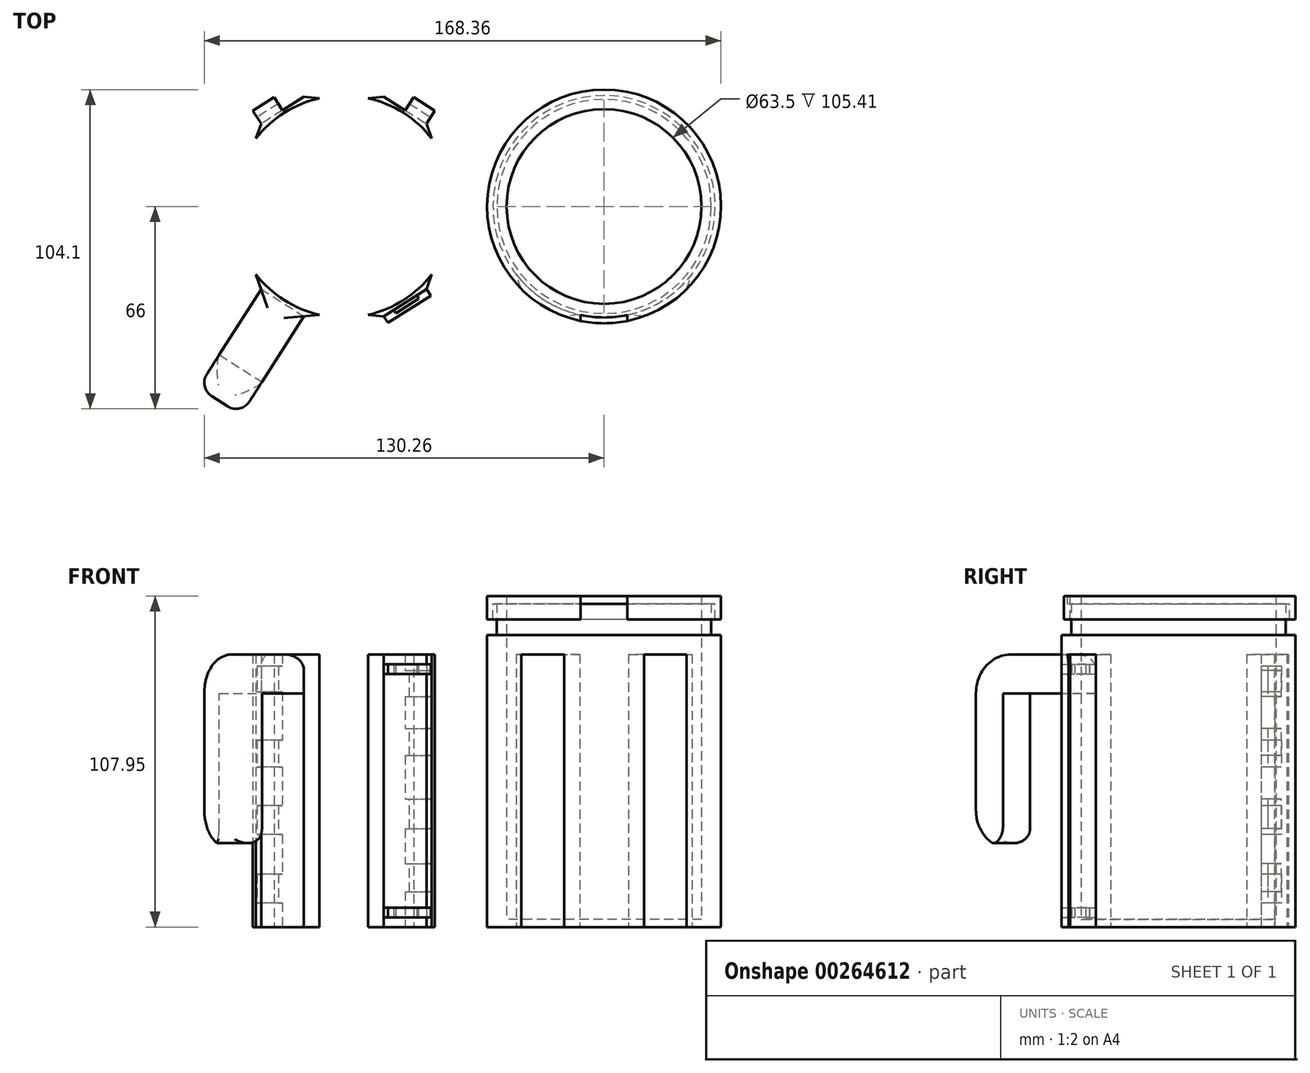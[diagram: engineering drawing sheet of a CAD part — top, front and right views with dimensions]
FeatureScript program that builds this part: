
annotation { "Feature Type Name" : "Feature", "Feature Type Description" : "" }
export const myFeature = defineFeature(function(context is Context, id is Id, definition is map)
    precondition{}
    {
        {
            var Q0;
            Q0=qCreatedBy(makeId("Top.planeOp"),FACE);
            var sketch = newSketch(context, id + "F0", { "sketchPlane" : qUnion([Q0])});
            skCircle(sketch, "E0", {"center": v(0, 0) * mm, "radius": 31.75 * mm});
            skCircle(sketch, "E1", {"center": v(0, 0) * mm, "radius": 38.1 * mm});
            skCircle(sketch, "E2", {"center": v(0, 0) * mm, "radius": 34.93 * mm});
            skCircle(sketch, "E3", {"center": v(0, 0) * mm, "radius": 36.2 * mm});
            skLineSegment(sketch, "E4", {"start": v(0, 0) * mm, "end": v(-26.94, -26.94) * mm});
            skLineSegment(sketch, "E5", {"start": v(0, 0) * mm, "end": v(26.94, -26.94) * mm});
            skLineSegment(sketch, "E6", {"start": v(0, 0) * mm, "end": v(-13.03, -35.8) * mm});
            skLineSegment(sketch, "E7", {"start": v(0, 0) * mm, "end": v(13.03, -35.8) * mm});
            skLineSegment(sketch, "E8", {"start": v(-26.94, -26.94) * mm, "end": v(-28.63, -22.15) * mm});
            skLineSegment(sketch, "E9", {"start": v(-7.98, -35.3) * mm, "end": v(-13.03, -35.8) * mm});
            skLineSegment(sketch, "E10", {"start": v(13.03, -35.8) * mm, "end": v(7.98, -35.3) * mm});
            skLineSegment(sketch, "E11", {"start": v(26.94, -26.94) * mm, "end": v(28.63, -22.15) * mm});
            skCircle(sketch, "E12", {"center": v(-84.78, 0) * mm, "radius": 38.1 * mm});
            skCircle(sketch, "E13", {"center": v(-84.78, 0) * mm, "radius": 36.2 * mm});
            skLineSegment(sketch, "E14", {"start": v(-84.78, 0) * mm, "end": v(-111.72, -26.94) * mm});
            skLineSegment(sketch, "E15", {"start": v(-84.78, 0) * mm, "end": v(-57.84, -26.94) * mm});
            skLineSegment(sketch, "E16", {"start": v(-84.78, 0) * mm, "end": v(-84.78, -38.1) * mm});
            skLineSegment(sketch, "E17", {"start": v(-84.78, 0) * mm, "end": v(-71.75, -35.8) * mm});
            skLineSegment(sketch, "E18", {"start": v(-84.78, 0) * mm, "end": v(-97.81, -35.8) * mm});
            skLineSegment(sketch, "E19", {"start": v(-111.72, -26.94) * mm, "end": v(-113.4, -22.15) * mm});
            skLineSegment(sketch, "E20", {"start": v(-97.81, -35.8) * mm, "end": v(-92.76, -35.3) * mm});
            skLineSegment(sketch, "E21", {"start": v(-71.75, -35.8) * mm, "end": v(-76.8, -35.3) * mm});
            skLineSegment(sketch, "E22", {"start": v(-57.84, -26.94) * mm, "end": v(-56.16, -22.15) * mm});
            skLineSegment(sketch, "E23", {"start": v(-111.72, -26.94) * mm, "end": v(-97.81, -35.8) * mm});
            skLineSegment(sketch, "E24", {"start": v(-71.75, -35.8) * mm, "end": v(-57.84, -26.94) * mm});
            skLineSegment(sketch, "E25", {"start": v(-84.78, 0) * mm, "end": v(-111.72, 26.94) * mm});
            skLineSegment(sketch, "E26", {"start": v(-84.78, 0) * mm, "end": v(-57.84, 26.94) * mm});
            skLineSegment(sketch, "E27", {"start": v(-84.78, 0) * mm, "end": v(-71.75, 35.8) * mm});
            skLineSegment(sketch, "E28", {"start": v(-84.78, 0) * mm, "end": v(-97.81, 35.8) * mm});
            skLineSegment(sketch, "E29", {"start": v(-84.78, 0) * mm, "end": v(-84.78, 38.1) * mm});
            skLineSegment(sketch, "E30", {"start": v(-111.72, 26.94) * mm, "end": v(-113.4, 22.15) * mm});
            skLineSegment(sketch, "E31", {"start": v(-97.81, 35.8) * mm, "end": v(-92.76, 35.3) * mm});
            skLineSegment(sketch, "E32", {"start": v(-71.75, 35.8) * mm, "end": v(-76.8, 35.3) * mm});
            skLineSegment(sketch, "E33", {"start": v(-57.84, 26.94) * mm, "end": v(-56.16, 22.15) * mm});
            skLineSegment(sketch, "E34", {"start": v(-57.84, 26.94) * mm, "end": v(-71.75, 35.8) * mm});
            skLineSegment(sketch, "E35", {"start": v(-97.81, 35.8) * mm, "end": v(-111.72, 26.94) * mm});
            skSolve(sketch);
        }
        {
            var Q0;
            Q0=makeQuery(id+"F0.imprint","IMPRINT",FACE,{"disambiguationData":[TD([[makeQuery(id+"F0.imprint","IMPRINT",EDGE,{"derivedFrom":sQuery(id+"F0.wireOp",EDGE,"E0")}),-1.0]])]});
            var Q1;
            {var subQ2=sQuery(id+"F0.wireOp",EDGE,"8zxYjvtb-MDoy-6YJJ-XKuE-w1UAtlA70Sip");Q1=makeQuery(id+"F0.imprint","IMPRINT",FACE,{"disambiguationData":[TD([[makeQuery(id+"F0.imprint","IMPRINT",EDGE,{"derivedFrom":subQ2}),1.0]])]});}
            var Q2;
            {var subQ0=sQuery(id+"F0.wireOp",EDGE,"h3sDWL1f-YZOR-unjp-TKPr-zdvw7zO6n5ZA");var subQ1=sQuery(id+"F0.wireOp",EDGE,"E1");var subQ2=makeQuery(id+"F0.imprint","INTERSECT",VERTEX,{"derivedFrom":[subQ1,subQ0]});Q2=makeQuery(id+"F0.imprint","IMPRINT",FACE,{"disambiguationData":[TD([[makeQuery(id+"F0.imprint","IMPRINT",EDGE,{"disambiguationData":[TD([[subQ2,1.0]])],"derivedFrom":subQ1}),1.0]])]});}
            var Q3;
            {var subQ0=sQuery(id+"F0.wireOp",EDGE,"h3sDWL1f-YZOR-unjp-TKPr-zdvw7zO6n5ZA");var subQ1=sQuery(id+"F0.wireOp",EDGE,"E1");var subQ2=makeQuery(id+"F0.imprint","INTERSECT",VERTEX,{"derivedFrom":[subQ1,subQ0]});Q3=makeQuery(id+"F0.imprint","IMPRINT",FACE,{"disambiguationData":[TD([[makeQuery(id+"F0.imprint","IMPRINT",EDGE,{"disambiguationData":[TD([[subQ2,-1.0]])],"derivedFrom":subQ1}),1.0]])]});}
            var Q4;
            {var subQ0=sQuery(id+"F0.wireOp",EDGE,"8zxYjvtb-MDoy-6YJJ-XKuE-w1UAtlA70Sip");Q4=makeQuery(id+"F0.imprint","IMPRINT",FACE,{"disambiguationData":[TD([[makeQuery(id+"F0.imprint","IMPRINT",EDGE,{"derivedFrom":subQ0}),-1.0]])]});}
            var Q5;
            {var subQ0=sQuery(id+"F0.wireOp",EDGE,"R7ShixpK-tb2N-bQR5-ACBT-eYuIy6adrrBf");var subQ1=sQuery(id+"F0.wireOp",EDGE,"E1");var subQ2=makeQuery(id+"F0.imprint","INTERSECT",VERTEX,{"derivedFrom":[subQ1,subQ0]});Q5=makeQuery(id+"F0.imprint","IMPRINT",FACE,{"disambiguationData":[TD([[makeQuery(id+"F0.imprint","IMPRINT",EDGE,{"disambiguationData":[TD([[subQ2,-1.0]])],"derivedFrom":subQ1}),1.0]])]});}
            var Q6;
            {var subQ0=sQuery(id+"F0.wireOp",EDGE,"C6yxxFIw-LrpI-xlVj-TdN5-gM4IXLVDDQ9a");Q6=makeQuery(id+"F0.imprint","IMPRINT",FACE,{"disambiguationData":[TD([[makeQuery(id+"F0.imprint","IMPRINT",EDGE,{"derivedFrom":subQ0}),-1.0]])]});}
            var Q7;
            {var subQ0=sQuery(id+"F0.wireOp",EDGE,"HXiYsXtY-R47m-jqzh-3tiA-JMCs7zAql3W5");var subQ1=sQuery(id+"F0.wireOp",EDGE,"E1");var subQ2=makeQuery(id+"F0.imprint","INTERSECT",VERTEX,{"derivedFrom":[subQ1,subQ0]});Q7=makeQuery(id+"F0.imprint","IMPRINT",FACE,{"disambiguationData":[TD([[makeQuery(id+"F0.imprint","IMPRINT",EDGE,{"disambiguationData":[TD([[subQ2,-1.0]])],"derivedFrom":subQ1}),1.0]])]});}
            var Q8;
            {var subQ0=sQuery(id+"F0.wireOp",EDGE,"HJ59A699-sTLV-QdIX-rFf9-DagDQaaTut5k");Q8=makeQuery(id+"F0.imprint","IMPRINT",FACE,{"disambiguationData":[TD([[makeQuery(id+"F0.imprint","IMPRINT",EDGE,{"derivedFrom":subQ0}),1.0]])]});}
            var Q9;
            Q9=makeQuery(id+"F0.imprint","IMPRINT",FACE,{"disambiguationData":[TD([[makeQuery(id+"F0.imprint","IMPRINT",EDGE,{"derivedFrom":sQuery(id+"F0.wireOp",EDGE,"E2")}),-1.0]])]});
            var Q10;
            {var subQ0=sQuery(id+"F0.wireOp",EDGE,"E8");Q10=makeQuery(id+"F0.imprint","IMPRINT",FACE,{"disambiguationData":[TD([[makeQuery(id+"F0.imprint","IMPRINT",EDGE,{"derivedFrom":subQ0}),-1.0]])]});}
            var Q11;
            {var subQ0=sQuery(id+"F0.wireOp",EDGE,"E9");Q11=makeQuery(id+"F0.imprint","IMPRINT",FACE,{"disambiguationData":[TD([[makeQuery(id+"F0.imprint","IMPRINT",EDGE,{"derivedFrom":subQ0}),-1.0]])]});}
            var Q12;
            {var subQ0=sQuery(id+"F0.wireOp",EDGE,"E10");Q12=makeQuery(id+"F0.imprint","IMPRINT",FACE,{"disambiguationData":[TD([[makeQuery(id+"F0.imprint","IMPRINT",EDGE,{"derivedFrom":subQ0}),-1.0]])]});}
            var Q13;
            {var subQ0=sQuery(id+"F0.wireOp",EDGE,"E11");Q13=makeQuery(id+"F0.imprint","IMPRINT",FACE,{"disambiguationData":[TD([[makeQuery(id+"F0.imprint","IMPRINT",EDGE,{"derivedFrom":subQ0}),1.0]])]});}
            var Q14;
            {var subQ5=sQuery(id+"F0.wireOp",EDGE,"E6");var subQ7=sQuery(id+"F0.wireOp",EDGE,"E2");var subQ8=makeQuery(id+"F0.imprint","INTERSECT",VERTEX,{"derivedFrom":[subQ7,subQ5]});Q14=makeQuery(id+"F0.imprint","IMPRINT",FACE,{"disambiguationData":[TD([[makeQuery(id+"F0.imprint","IMPRINT",EDGE,{"disambiguationData":[TD([[subQ8,-1.0]])],"derivedFrom":subQ7}),-1.0]])]});}
            var Q15;
            {var subQ5=sQuery(id+"F0.wireOp",EDGE,"E4");var subQ7=sQuery(id+"F0.wireOp",EDGE,"E2");var subQ8=makeQuery(id+"F0.imprint","INTERSECT",VERTEX,{"derivedFrom":[subQ7,subQ5]});Q15=makeQuery(id+"F0.imprint","IMPRINT",FACE,{"disambiguationData":[TD([[makeQuery(id+"F0.imprint","IMPRINT",EDGE,{"disambiguationData":[TD([[subQ8,1.0]])],"derivedFrom":subQ7}),-1.0]])]});}
            extrude(context, id + "F1", {"entities" : qUnion([Q0, Q1, Q2, Q3, Q4, Q5, Q6, Q7, Q8, Q9, Q10, Q11, Q12, Q13, Q14, Q15]), "depth" : 95.25 * mm});
        }
        {
            var Q0;
            Q0=makeQuery(id+"F0.imprint","IMPRINT",FACE,{"disambiguationData":[TD([[makeQuery(id+"F0.imprint","IMPRINT",EDGE,{"derivedFrom":sQuery(id+"F0.wireOp",EDGE,"E0")}),-1.0]])]});
            extrude(context, id + "F2", {"entities" : qUnion([Q0]), "operationType" : NewBodyOperationType.ADD, "depth" : 107.95 * mm});
        }
        {
            var Q0;
            Q0=makeQuery(id+"F2.opExtrude","CAP_FACE",FACE,{"disambiguationData":[OSD([sQuery(id+"F0.wireOp",EDGE,"E0"),sQuery(id+"F0.wireOp",EDGE,"E2")])],"isStart":false});
            var sketch = newSketch(context, id + "F3", { "sketchPlane" : qUnion([Q0])});
            skCircle(sketch, "E36", {"center": v(0, 0) * mm, "radius": 36.2 * mm});
            skCircle(sketch, "E37", {"center": v(0, 0) * mm, "radius": 38.1 * mm});
            skLineSegment(sketch, "E38.left", {"start": v(-7.62, -35.38) * mm, "end": v(-7.62, -37.33) * mm});
            skLineSegment(sketch, "E38.right", {"start": v(7.62, -35.38) * mm, "end": v(7.62, -37.33) * mm});
            skPoint(sketch, "E39.orphan", {"position": v(7.62, 0) * mm});
            skPoint(sketch, "E40.orphan", {"position": v(-7.62, 0) * mm});
            skSolve(sketch);
        }
        {
            var Q0;
            Q0=makeQuery(id+"F3.imprint","IMPRINT",FACE,{"disambiguationData":[TD([[makeQuery(id+"F3.imprint","IMPRINT",EDGE,{"derivedFrom":sQuery(id+"F3.wireOp",EDGE,"E36")}),1.0]])]});
            extrude(context, id + "F4", {"entities" : qUnion([Q0]), "operationType" : NewBodyOperationType.ADD, "oppositeDirection" : true, "depth" : 2.54 * mm});
        }
        {
            var Q0;
            Q0=makeQuery(id+"F3.imprint","IMPRINT",FACE,{"disambiguationData":[TD([[makeQuery(id+"F3.imprint","IMPRINT",EDGE,{"derivedFrom":sQuery(id+"F3.wireOp",EDGE,"E36")}),-1.0]])]});
            extrude(context, id + "F5", {"entities" : qUnion([Q0]), "operationType" : NewBodyOperationType.ADD, "oppositeDirection" : true, "depth" : 7.62 * mm});
        }
        {
            var Q0;
            {var subQ0=sQuery(id+"F3.wireOp",EDGE,"E38.left");Q0=makeQuery(id+"F3.imprint","IMPRINT",FACE,{"disambiguationData":[TD([[makeQuery(id+"F3.imprint","IMPRINT",EDGE,{"derivedFrom":subQ0}),1.0]])]});}
            extrude(context, id + "F6", {"entities" : qUnion([Q0]), "operationType" : NewBodyOperationType.REMOVE, "oppositeDirection" : true, "depth" : 7.62 * mm});
        }
        {
            var Q0;
            {var subQ0=sQuery(id+"F0.wireOp",EDGE,"E8");Q0=makeQuery(id+"F0.imprint","IMPRINT",FACE,{"disambiguationData":[TD([[makeQuery(id+"F0.imprint","IMPRINT",EDGE,{"derivedFrom":subQ0}),-1.0]])]});}
            var Q1;
            {var subQ0=sQuery(id+"F0.wireOp",EDGE,"E4");var subQ5=sQuery(id+"F0.wireOp",EDGE,"E3");var subQ6=makeQuery(id+"F0.imprint","INTERSECT",VERTEX,{"derivedFrom":[subQ5,subQ0]});Q1=makeQuery(id+"F0.imprint","IMPRINT",FACE,{"disambiguationData":[TD([[makeQuery(id+"F0.imprint","IMPRINT",EDGE,{"disambiguationData":[TD([[subQ6,-1.0]])],"derivedFrom":subQ5}),-1.0]])]});}
            var Q2;
            {var subQ0=sQuery(id+"F0.wireOp",EDGE,"E9");Q2=makeQuery(id+"F0.imprint","IMPRINT",FACE,{"disambiguationData":[TD([[makeQuery(id+"F0.imprint","IMPRINT",EDGE,{"derivedFrom":subQ0}),-1.0]])]});}
            var Q3;
            {var subQ0=sQuery(id+"F0.wireOp",EDGE,"E10");Q3=makeQuery(id+"F0.imprint","IMPRINT",FACE,{"disambiguationData":[TD([[makeQuery(id+"F0.imprint","IMPRINT",EDGE,{"derivedFrom":subQ0}),-1.0]])]});}
            var Q4;
            {var subQ3=sQuery(id+"F0.wireOp",EDGE,"E7");var subQ5=sQuery(id+"F0.wireOp",EDGE,"E3");var subQ6=makeQuery(id+"F0.imprint","INTERSECT",VERTEX,{"derivedFrom":[subQ5,subQ3]});Q4=makeQuery(id+"F0.imprint","IMPRINT",FACE,{"disambiguationData":[TD([[makeQuery(id+"F0.imprint","IMPRINT",EDGE,{"disambiguationData":[TD([[subQ6,-1.0]])],"derivedFrom":subQ5}),-1.0]])]});}
            var Q5;
            {var subQ0=sQuery(id+"F0.wireOp",EDGE,"E11");Q5=makeQuery(id+"F0.imprint","IMPRINT",FACE,{"disambiguationData":[TD([[makeQuery(id+"F0.imprint","IMPRINT",EDGE,{"derivedFrom":subQ0}),1.0]])]});}
            extrude(context, id + "F7", {"entities" : qUnion([Q0, Q1, Q2, Q3, Q4, Q5]), "operationType" : NewBodyOperationType.REMOVE, "depth" : 88.9 * mm});
        }
        {
            var Q0;
            {var subQ0=sQuery(id+"F0.wireOp",EDGE,"E14");var subQ5=sQuery(id+"F0.wireOp",EDGE,"E13");var subQ6=makeQuery(id+"F0.imprint","INTERSECT",VERTEX,{"derivedFrom":[subQ5,subQ0]});Q0=makeQuery(id+"F0.imprint","IMPRINT",FACE,{"disambiguationData":[TD([[makeQuery(id+"F0.imprint","IMPRINT",EDGE,{"disambiguationData":[TD([[subQ6,-1.0]])],"derivedFrom":subQ5}),-1.0]])]});}
            var Q1;
            {var subQ0=sQuery(id+"F0.wireOp",EDGE,"E19");Q1=makeQuery(id+"F0.imprint","IMPRINT",FACE,{"disambiguationData":[TD([[makeQuery(id+"F0.imprint","IMPRINT",EDGE,{"derivedFrom":subQ0}),-1.0]])]});}
            var Q2;
            {var subQ0=sQuery(id+"F0.wireOp",EDGE,"E20");Q2=makeQuery(id+"F0.imprint","IMPRINT",FACE,{"disambiguationData":[TD([[makeQuery(id+"F0.imprint","IMPRINT",EDGE,{"derivedFrom":subQ0}),1.0]])]});}
            var Q3;
            {var subQ0=sQuery(id+"F0.wireOp",EDGE,"E21");Q3=makeQuery(id+"F0.imprint","IMPRINT",FACE,{"disambiguationData":[TD([[makeQuery(id+"F0.imprint","IMPRINT",EDGE,{"derivedFrom":subQ0}),-1.0]])]});}
            var Q4;
            {var subQ3=sQuery(id+"F0.wireOp",EDGE,"E17");var subQ5=sQuery(id+"F0.wireOp",EDGE,"E13");var subQ7=makeQuery(id+"F0.imprint","INTERSECT",VERTEX,{"derivedFrom":[subQ5,subQ3]});Q4=makeQuery(id+"F0.imprint","IMPRINT",FACE,{"disambiguationData":[TD([[makeQuery(id+"F0.imprint","IMPRINT",EDGE,{"disambiguationData":[TD([[subQ7,-1.0]])],"derivedFrom":subQ5}),-1.0]])]});}
            var Q5;
            {var subQ0=sQuery(id+"F0.wireOp",EDGE,"E22");Q5=makeQuery(id+"F0.imprint","IMPRINT",FACE,{"disambiguationData":[TD([[makeQuery(id+"F0.imprint","IMPRINT",EDGE,{"derivedFrom":subQ0}),1.0]])]});}
            extrude(context, id + "F8", {"entities" : qUnion([Q0, Q1, Q2, Q3, Q4, Q5]), "operationType" : NewBodyOperationType.ADD, "depth" : 88.9 * mm});
        }
        {
            var Q0;
            Q0=makeQuery(id+"F8.opExtrude","SWEPT_FACE",FACE,{"disambiguationData":[OSD([sQuery(id+"F0.wireOp",EDGE,"E23")])]});
            var sketch = newSketch(context, id + "F9", { "sketchPlane" : qUnion([Q0])});
            skLineSegment(sketch, "E41", {"start": v(-79.75, 76.2) * mm, "end": v(-63.26, 76.2) * mm});
            skSolve(sketch);
        }
        {
            var Q0;
            {var subQ0=sQuery(id+"F9.wireOp",EDGE,"E41");Q0=makeQuery(id+"F9.imprint","IMPRINT",FACE,{"disambiguationData":[TD([[makeQuery(id+"F9.imprint","IMPRINT",EDGE,{"derivedFrom":subQ0}),1.0]])]});}
            extrude(context, id + "F10", {"entities" : qUnion([Q0]), "operationType" : NewBodyOperationType.ADD, "depth" : 38.1 * mm});
        }
        {
            var Q0;
            Q0=makeQuery(id+"F10.opExtrude","SWEPT_FACE",FACE,{"disambiguationData":[OSD([sQuery(id+"F9.wireOp",EDGE,"E41")])]});
            var sketch = newSketch(context, id + "F11", { "sketchPlane" : qUnion([Q0])});
            skLineSegment(sketch, "E42", {"start": v(-125.37, 48.36) * mm, "end": v(-111.46, 57.22) * mm});
            skSolve(sketch);
        }
        {
            var Q0;
            {var subQ0=sQuery(id+"F11.wireOp",EDGE,"E42");Q0=makeQuery(id+"F11.imprint","IMPRINT",FACE,{"disambiguationData":[TD([[makeQuery(id+"F11.imprint","IMPRINT",EDGE,{"derivedFrom":subQ0}),1.0]])]});}
            extrude(context, id + "F12", {"entities" : qUnion([Q0]), "operationType" : NewBodyOperationType.ADD, "depth" : 50.8 * mm});
        }
        {
            var Q0;
            Q0=makeQuery(id+"F10.opExtrude","CAP_EDGE",EDGE,{"disambiguationData":[OSD([sQuery(id+"F9.wireOp",EDGE,"E41")])],"isStart":true});
            var Q1;
            Q1=makeQuery(id+"F12.opExtrude","CAP_EDGE",EDGE,{"disambiguationData":[OSD([sQuery(id+"F11.wireOp",EDGE,"E42")])],"isStart":true});
            var Q2;
            Q2=makeQuery(id+"F10.opExtrude","CAP_EDGE",EDGE,{"disambiguationData":[OSD([sQuery(id+"F0.wireOp",EDGE,"E23")])],"isStart":false});
            var Q3;
            Q3=makeQuery(id+"F12.opExtrude","CAP_EDGE",EDGE,{"disambiguationData":[OSD([sQuery(id+"F9.wireOp",EDGE,"E41")])],"isStart":false});
            fillet(context, id + "F13", {"entities" : qUnion([Q0, Q1, Q2, Q3]), "radius" : 12.7 * mm, "tangentPropagation" : true, "allowEdgeOverflow" : false});
        }
        {
            var Q0;
            {var subQ0=sQuery(id+"F0.wireOp",EDGE,"E23");var subQ1=sQuery(id+"F0.wireOp",EDGE,"E19");var subQ2=sQuery(id+"F0.wireOp",EDGE,"E14");var subQ3=sQuery(id+"F0.wireOp",EDGE,"E12");Q0=makeQuery(id+"F12.boolean.opBoolean","MERGE",EDGE,{"derivedFrom":[makeQuery(id+"F10.opExtrude","CAP_EDGE",EDGE,{"disambiguationData":[OSD([subQ3,subQ2,subQ1,subQ0])],"isStart":false}),makeQuery(id+"F12.opExtrude","SWEPT_EDGE",EDGE,{"disambiguationData":[OSD([subQ3,subQ2,subQ1,subQ0,sQuery(id+"F9.wireOp",EDGE,"E41")])]})]});}
            var Q1;
            {var subQ0=sQuery(id+"F0.wireOp",EDGE,"E23");var subQ1=sQuery(id+"F0.wireOp",EDGE,"E20");var subQ2=sQuery(id+"F0.wireOp",EDGE,"E18");var subQ3=sQuery(id+"F0.wireOp",EDGE,"E12");Q1=makeQuery(id+"F12.boolean.opBoolean","MERGE",EDGE,{"derivedFrom":[makeQuery(id+"F10.opExtrude","CAP_EDGE",EDGE,{"disambiguationData":[OSD([subQ3,subQ2,subQ1,subQ0])],"isStart":false}),makeQuery(id+"F12.opExtrude","SWEPT_EDGE",EDGE,{"disambiguationData":[OSD([subQ3,subQ2,subQ1,subQ0,sQuery(id+"F9.wireOp",EDGE,"E41")])]})]});}
            var Q2;
            {var subQ0=sQuery(id+"F9.wireOp",EDGE,"E41");var subQ1=sQuery(id+"F0.wireOp",EDGE,"E23");var subQ2=sQuery(id+"F0.wireOp",EDGE,"E19");var subQ3=sQuery(id+"F0.wireOp",EDGE,"E14");var subQ4=sQuery(id+"F0.wireOp",EDGE,"E12");Q2=makeQuery(id+"F13.opFillet","BLEND_EDGE",EDGE,{"blendedFrom":[makeQuery(id+"F10.opExtrude","CAP_EDGE",EDGE,{"disambiguationData":[OSD([subQ0])],"isStart":true}),makeQuery(id+"F12.boolean.opBoolean","MERGE",FACE,{"derivedFrom":[makeQuery(id+"F10.opExtrude","SWEPT_FACE",FACE,{"disambiguationData":[OSD([subQ4,subQ3,subQ2,subQ1])]}),makeQuery(id+"F12.opExtrude","SWEPT_FACE",FACE,{"disambiguationData":[OSD([subQ4,subQ3,subQ2,subQ1,subQ0])]})]})],"blendedInto":[makeQuery(id+"F12.boolean.opBoolean","MERGE",FACE,{"derivedFrom":[makeQuery(id+"F10.opExtrude","SWEPT_FACE",FACE,{"disambiguationData":[OSD([subQ4,subQ3,subQ2,subQ1])]}),makeQuery(id+"F12.opExtrude","SWEPT_FACE",FACE,{"disambiguationData":[OSD([subQ4,subQ3,subQ2,subQ1,subQ0])]})]})]});}
            var Q3;
            Q3=makeQuery(id+"F13.opFillet","BLEND_EDGE",EDGE,{"blendedFrom":[makeQuery(id+"F12.opExtrude","CAP_EDGE",EDGE,{"disambiguationData":[OSD([sQuery(id+"F9.wireOp",EDGE,"E41")])],"isStart":false}),makeQuery(id+"F12.opExtrude","SWEPT_FACE",FACE,{"disambiguationData":[OSD([sQuery(id+"F11.wireOp",EDGE,"E42")])]})],"blendedInto":[makeQuery(id+"F12.opExtrude","SWEPT_FACE",FACE,{"disambiguationData":[OSD([sQuery(id+"F11.wireOp",EDGE,"E42")])]})]});
            fillet(context, id + "F14", {"entities" : qUnion([Q0, Q1, Q2, Q3]), "radius" : 5.08 * mm, "tangentPropagation" : true, "allowEdgeOverflow" : false});
        }
        {
            var Q0;
            Q0=makeQuery(id+"F8.opExtrude","SWEPT_FACE",FACE,{"disambiguationData":[OSD([sQuery(id+"F0.wireOp",EDGE,"E24")])]});
            var sketch = newSketch(context, id + "F15", { "sketchPlane" : qUnion([Q0])});
            skLineSegment(sketch, "E43", {"start": v(-75.94, 88.9) * mm, "end": v(-75.94, 82.55) * mm});
            skLineSegment(sketch, "E44", {"start": v(-67.07, 88.9) * mm, "end": v(-67.07, 82.55) * mm});
            skLineSegment(sketch, "E45", {"start": v(-79.75, 82.55) * mm, "end": v(-63.26, 82.55) * mm});
            skLineSegment(sketch, "E46", {"start": v(-79.75, 85.73) * mm, "end": v(-63.26, 85.73) * mm});
            skPoint(sketch, "E46.startSnap0", {"position": v(-75.94, 85.73) * mm});
            skLineSegment(sketch, "E47", {"start": v(-79.75, 6.35) * mm, "end": v(-63.26, 6.35) * mm});
            skLineSegment(sketch, "E48", {"start": v(-75.94, 6.35) * mm, "end": v(-75.94, 0) * mm});
            skLineSegment(sketch, "E49", {"start": v(-67.07, 6.35) * mm, "end": v(-67.07, 0) * mm});
            skLineSegment(sketch, "E50", {"start": v(-67.07, 3.18) * mm, "end": v(-63.26, 3.17) * mm});
            skLineSegment(sketch, "E51", {"start": v(-67.07, 3.18) * mm, "end": v(-79.75, 3.17) * mm});
            skSolve(sketch);
        }
        {
            var Q0;
            {var subQ0=sQuery(id+"F15.wireOp",EDGE,"E45");var subQ1=sQuery(id+"F15.wireOp",EDGE,"E43");var subQ2=makeQuery(id+"F15.imprint","INTERSECT",VERTEX,{"derivedFrom":[subQ1,subQ0]});Q0=makeQuery(id+"F15.imprint","IMPRINT",FACE,{"disambiguationData":[TD([[makeQuery(id+"F15.imprint","IMPRINT",EDGE,{"disambiguationData":[TD([[subQ2,1.0]])],"derivedFrom":subQ1}),-1.0]])]});}
            var Q1;
            {var subQ0=sQuery(id+"F15.wireOp",EDGE,"E45");var subQ1=sQuery(id+"F15.wireOp",EDGE,"E44");var subQ2=makeQuery(id+"F15.imprint","INTERSECT",VERTEX,{"derivedFrom":[subQ1,subQ0]});Q1=makeQuery(id+"F15.imprint","IMPRINT",FACE,{"disambiguationData":[TD([[makeQuery(id+"F15.imprint","IMPRINT",EDGE,{"disambiguationData":[TD([[subQ2,1.0]])],"derivedFrom":subQ1}),1.0]])]});}
            extrude(context, id + "F16", {"entities" : qUnion([Q0, Q1]), "operationType" : NewBodyOperationType.ADD, "depth" : 2.54 * mm});
        }
        {
            var Q0;
            Q0=makeQuery(id+"F16.opExtrude","SWEPT_FACE",FACE,{"disambiguationData":[OSD([sQuery(id+"F15.wireOp",EDGE,"E43")])]});
            var sketch = newSketch(context, id + "F17", { "sketchPlane" : qUnion([Q0])});
            skLineSegment(sketch, "E52", {"start": v(7.09, 85.73) * mm, "end": v(7.09, 82.55) * mm});
            skSolve(sketch);
        }
        {
            var Q0;
            {var subQ0=sQuery(id+"F17.wireOp",EDGE,"E52");Q0=makeQuery(id+"F17.imprint","IMPRINT",FACE,{"disambiguationData":[TD([[makeQuery(id+"F17.imprint","IMPRINT",EDGE,{"derivedFrom":subQ0}),-1.0]])]});}
            extrude(context, id + "F18", {"entities" : qUnion([Q0]), "operationType" : NewBodyOperationType.ADD, "depth" : 10.16 * mm});
        }
        {
            var Q0;
            {var subQ0=sQuery(id+"F15.wireOp",EDGE,"E47");var subQ3=sQuery(id+"F15.wireOp",EDGE,"E48");var subQ4=makeQuery(id+"F15.imprint","INTERSECT",VERTEX,{"derivedFrom":[subQ0,subQ3]});Q0=makeQuery(id+"F15.imprint","IMPRINT",FACE,{"disambiguationData":[TD([[makeQuery(id+"F15.imprint","IMPRINT",EDGE,{"disambiguationData":[TD([[subQ4,-1.0]])],"derivedFrom":subQ3}),-1.0]])]});}
            var Q1;
            {var subQ5=sQuery(id+"F15.wireOp",EDGE,"E50");Q1=makeQuery(id+"F15.imprint","IMPRINT",FACE,{"disambiguationData":[TD([[makeQuery(id+"F15.imprint","IMPRINT",EDGE,{"derivedFrom":subQ5}),1.0]])]});}
            extrude(context, id + "F19", {"entities" : qUnion([Q0, Q1]), "operationType" : NewBodyOperationType.ADD, "depth" : 2.54 * mm});
        }
        {
            var Q0;
            Q0=makeQuery(id+"F19.opExtrude","SWEPT_FACE",FACE,{"disambiguationData":[OSD([sQuery(id+"F15.wireOp",EDGE,"E48")])]});
            var sketch = newSketch(context, id + "F20", { "sketchPlane" : qUnion([Q0])});
            skLineSegment(sketch, "E53", {"start": v(7.09, 6.35) * mm, "end": v(7.09, 3.17) * mm});
            skSolve(sketch);
        }
        {
            var Q0;
            {var subQ0=sQuery(id+"F20.wireOp",EDGE,"E53");Q0=makeQuery(id+"F20.imprint","IMPRINT",FACE,{"disambiguationData":[TD([[makeQuery(id+"F20.imprint","IMPRINT",EDGE,{"derivedFrom":subQ0}),-1.0]])]});}
            extrude(context, id + "F21", {"entities" : qUnion([Q0]), "operationType" : NewBodyOperationType.ADD, "depth" : 10.16 * mm});
        }
        {
            var Q0;
            {var subQ3=sQuery(id+"F0.wireOp",EDGE,"E28");var subQ5=sQuery(id+"F0.wireOp",EDGE,"E13");var subQ6=makeQuery(id+"F0.imprint","INTERSECT",VERTEX,{"derivedFrom":[subQ5,subQ3]});Q0=makeQuery(id+"F0.imprint","IMPRINT",FACE,{"disambiguationData":[TD([[makeQuery(id+"F0.imprint","IMPRINT",EDGE,{"disambiguationData":[TD([[subQ6,-1.0]])],"derivedFrom":subQ5}),-1.0]])]});}
            var Q1;
            {var subQ0=sQuery(id+"F0.wireOp",EDGE,"E30");Q1=makeQuery(id+"F0.imprint","IMPRINT",FACE,{"disambiguationData":[TD([[makeQuery(id+"F0.imprint","IMPRINT",EDGE,{"derivedFrom":subQ0}),1.0]])]});}
            var Q2;
            {var subQ0=sQuery(id+"F0.wireOp",EDGE,"E31");Q2=makeQuery(id+"F0.imprint","IMPRINT",FACE,{"disambiguationData":[TD([[makeQuery(id+"F0.imprint","IMPRINT",EDGE,{"derivedFrom":subQ0}),-1.0]])]});}
            var Q3;
            {var subQ0=sQuery(id+"F0.wireOp",EDGE,"E32");Q3=makeQuery(id+"F0.imprint","IMPRINT",FACE,{"disambiguationData":[TD([[makeQuery(id+"F0.imprint","IMPRINT",EDGE,{"derivedFrom":subQ0}),1.0]])]});}
            var Q4;
            {var subQ0=sQuery(id+"F0.wireOp",EDGE,"E26");var subQ5=sQuery(id+"F0.wireOp",EDGE,"E13");var subQ6=makeQuery(id+"F0.imprint","INTERSECT",VERTEX,{"derivedFrom":[subQ5,subQ0]});Q4=makeQuery(id+"F0.imprint","IMPRINT",FACE,{"disambiguationData":[TD([[makeQuery(id+"F0.imprint","IMPRINT",EDGE,{"disambiguationData":[TD([[subQ6,-1.0]])],"derivedFrom":subQ5}),-1.0]])]});}
            var Q5;
            {var subQ0=sQuery(id+"F0.wireOp",EDGE,"E33");Q5=makeQuery(id+"F0.imprint","IMPRINT",FACE,{"disambiguationData":[TD([[makeQuery(id+"F0.imprint","IMPRINT",EDGE,{"derivedFrom":subQ0}),-1.0]])]});}
            extrude(context, id + "F22", {"entities" : qUnion([Q0, Q1, Q2, Q3, Q4, Q5]), "depth" : 88.9 * mm});
        }
        {
            var Q0;
            Q0=makeQuery(id+"F22.opExtrude","SWEPT_FACE",FACE,{"disambiguationData":[OSD([sQuery(id+"F0.wireOp",EDGE,"E35")])]});
            var sketch = newSketch(context, id + "F23", { "sketchPlane" : qUnion([Q0])});
            skLineSegment(sketch, "E54", {"start": v(71.5, 88.9) * mm, "end": v(71.5, 0) * mm});
            skSolve(sketch);
        }
        {
            var Q0;
            {var subQ0=sQuery(id+"F23.wireOp",EDGE,"E54");Q0=makeQuery(id+"F23.imprint","IMPRINT",FACE,{"disambiguationData":[TD([[makeQuery(id+"F23.imprint","IMPRINT",EDGE,{"derivedFrom":subQ0}),1.0]])]});}
            extrude(context, id + "F24", {"entities" : qUnion([Q0]), "operationType" : NewBodyOperationType.ADD, "depth" : 5.08 * mm});
        }
        {
            var Q0;
            Q0=makeQuery(id+"F24.opExtrude","SWEPT_FACE",FACE,{"disambiguationData":[OSD([sQuery(id+"F0.wireOp",EDGE,"E12"),sQuery(id+"F0.wireOp",EDGE,"E25"),sQuery(id+"F0.wireOp",EDGE,"E30"),sQuery(id+"F0.wireOp",EDGE,"E35")])]});
            var sketch = newSketch(context, id + "F25", { "sketchPlane" : qUnion([Q0])});
            skLineSegment(sketch, "E55", {"start": v(-85.3, 88.9) * mm, "end": v(-85.3, 0) * mm});
            skLineSegment(sketch, "E56", {"start": v(-85.3, 85.05) * mm, "end": v(-82.75, 85.05) * mm});
            skLineSegment(sketch, "E57", {"start": v(-85.3, 76.63) * mm, "end": v(-82.75, 76.63) * mm});
            skLineSegment(sketch, "E58", {"start": v(-85.3, 60.95) * mm, "end": v(-82.75, 60.95) * mm});
            skLineSegment(sketch, "E59", {"start": v(-85.3, 52.14) * mm, "end": v(-82.75, 52.14) * mm});
            skLineSegment(sketch, "E60", {"start": v(-85.3, 39.6) * mm, "end": v(-82.75, 39.6) * mm});
            skLineSegment(sketch, "E61", {"start": v(-85.3, 30.19) * mm, "end": v(-82.75, 30.19) * mm});
            skLineSegment(sketch, "E62", {"start": v(-85.3, 17.26) * mm, "end": v(-82.75, 17.26) * mm});
            skLineSegment(sketch, "E63", {"start": v(-85.3, 7.86) * mm, "end": v(-82.75, 7.86) * mm});
            skSolve(sketch);
        }
        {
            var Q0;
            {var subQ0=sQuery(id+"F25.wireOp",EDGE,"E58");Q0=makeQuery(id+"F25.imprint","IMPRINT",FACE,{"disambiguationData":[TD([[makeQuery(id+"F25.imprint","IMPRINT",EDGE,{"derivedFrom":subQ0}),-1.0]])]});}
            var Q1;
            {var subQ0=sQuery(id+"F25.wireOp",EDGE,"E56");Q1=makeQuery(id+"F25.imprint","IMPRINT",FACE,{"disambiguationData":[TD([[makeQuery(id+"F25.imprint","IMPRINT",EDGE,{"derivedFrom":subQ0}),-1.0]])]});}
            var Q2;
            {var subQ0=sQuery(id+"F25.wireOp",EDGE,"E60");Q2=makeQuery(id+"F25.imprint","IMPRINT",FACE,{"disambiguationData":[TD([[makeQuery(id+"F25.imprint","IMPRINT",EDGE,{"derivedFrom":subQ0}),-1.0]])]});}
            var Q3;
            {var subQ0=sQuery(id+"F25.wireOp",EDGE,"E62");Q3=makeQuery(id+"F25.imprint","IMPRINT",FACE,{"disambiguationData":[TD([[makeQuery(id+"F25.imprint","IMPRINT",EDGE,{"derivedFrom":subQ0}),-1.0]])]});}
            extrude(context, id + "F26", {"entities" : qUnion([Q0, Q1, Q2, Q3]), "operationType" : NewBodyOperationType.REMOVE, "oppositeDirection" : true, "depth" : 10.16 * mm});
        }
        {
            var Q0;
            Q0=makeQuery(id+"F22.opExtrude","SWEPT_FACE",FACE,{"disambiguationData":[OSD([sQuery(id+"F0.wireOp",EDGE,"E34")])]});
            var sketch = newSketch(context, id + "F27", { "sketchPlane" : qUnion([Q0])});
            skLineSegment(sketch, "E64", {"start": v(71.5, 88.9) * mm, "end": v(71.5, 0) * mm});
            skSolve(sketch);
        }
        {
            var Q0;
            {var subQ0=sQuery(id+"F27.wireOp",EDGE,"E64");Q0=makeQuery(id+"F27.imprint","IMPRINT",FACE,{"disambiguationData":[TD([[makeQuery(id+"F27.imprint","IMPRINT",EDGE,{"derivedFrom":subQ0}),-1.0]])]});}
            extrude(context, id + "F28", {"entities" : qUnion([Q0]), "operationType" : NewBodyOperationType.ADD, "depth" : 5.08 * mm});
        }
        {
            var Q0;
            Q0=makeQuery(id+"F28.opExtrude","SWEPT_FACE",FACE,{"disambiguationData":[OSD([sQuery(id+"F0.wireOp",EDGE,"E12"),sQuery(id+"F0.wireOp",EDGE,"E26"),sQuery(id+"F0.wireOp",EDGE,"E33"),sQuery(id+"F0.wireOp",EDGE,"E34")])]});
            var sketch = newSketch(context, id + "F29", { "sketchPlane" : qUnion([Q0])});
            skLineSegment(sketch, "E65", {"start": v(-5.82, 88.9) * mm, "end": v(-5.82, 0) * mm});
            skLineSegment(sketch, "E66", {"start": v(-5.82, 83.59) * mm, "end": v(-8.36, 83.59) * mm});
            skLineSegment(sketch, "E67", {"start": v(-5.82, 75.09) * mm, "end": v(-8.36, 75.09) * mm});
            skLineSegment(sketch, "E68", {"start": v(-5.82, 64.7) * mm, "end": v(-8.36, 64.7) * mm});
            skLineSegment(sketch, "E69", {"start": v(-5.82, 55.93) * mm, "end": v(-8.36, 55.93) * mm});
            skLineSegment(sketch, "E70", {"start": v(-5.82, 41.75) * mm, "end": v(-8.36, 41.75) * mm});
            skLineSegment(sketch, "E71", {"start": v(-5.82, 32.07) * mm, "end": v(-8.36, 32.07) * mm});
            skLineSegment(sketch, "E72", {"start": v(-5.82, 20.64) * mm, "end": v(-8.36, 20.64) * mm});
            skLineSegment(sketch, "E73", {"start": v(-5.82, 11.54) * mm, "end": v(-8.36, 11.54) * mm});
            skSolve(sketch);
        }
        {
            var Q0;
            {var subQ0=sQuery(id+"F29.wireOp",EDGE,"E72");Q0=makeQuery(id+"F29.imprint","IMPRINT",FACE,{"disambiguationData":[TD([[makeQuery(id+"F29.imprint","IMPRINT",EDGE,{"derivedFrom":subQ0}),1.0]])]});}
            var Q1;
            {var subQ0=sQuery(id+"F29.wireOp",EDGE,"E70");Q1=makeQuery(id+"F29.imprint","IMPRINT",FACE,{"disambiguationData":[TD([[makeQuery(id+"F29.imprint","IMPRINT",EDGE,{"derivedFrom":subQ0}),1.0]])]});}
            var Q2;
            {var subQ0=sQuery(id+"F29.wireOp",EDGE,"E68");Q2=makeQuery(id+"F29.imprint","IMPRINT",FACE,{"disambiguationData":[TD([[makeQuery(id+"F29.imprint","IMPRINT",EDGE,{"derivedFrom":subQ0}),1.0]])]});}
            var Q3;
            {var subQ0=sQuery(id+"F29.wireOp",EDGE,"E66");Q3=makeQuery(id+"F29.imprint","IMPRINT",FACE,{"disambiguationData":[TD([[makeQuery(id+"F29.imprint","IMPRINT",EDGE,{"derivedFrom":subQ0}),1.0]])]});}
            extrude(context, id + "F30", {"entities" : qUnion([Q0, Q1, Q2, Q3]), "operationType" : NewBodyOperationType.REMOVE, "oppositeDirection" : true, "depth" : 10.16 * mm});
        }
        {
            var Q0;
            {var subQ0=sQuery(id+"F0.wireOp",EDGE,"E4");var subQ1=sQuery(id+"F0.wireOp",EDGE,"E0");var subQ2=makeQuery(id+"F0.imprint","INTERSECT",VERTEX,{"derivedFrom":[subQ1,subQ0]});Q0=makeQuery(id+"F0.imprint","IMPRINT",FACE,{"disambiguationData":[TD([[makeQuery(id+"F0.imprint","IMPRINT",EDGE,{"disambiguationData":[TD([[subQ2,1.0]])],"derivedFrom":subQ1}),1.0]])]});}
            var Q1;
            {var subQ0=sQuery(id+"F0.wireOp",EDGE,"E6");var subQ1=sQuery(id+"F0.wireOp",EDGE,"E0");var subQ2=makeQuery(id+"F0.imprint","INTERSECT",VERTEX,{"derivedFrom":[subQ1,subQ0]});Q1=makeQuery(id+"F0.imprint","IMPRINT",FACE,{"disambiguationData":[TD([[makeQuery(id+"F0.imprint","IMPRINT",EDGE,{"disambiguationData":[TD([[subQ2,1.0]])],"derivedFrom":subQ1}),1.0]])]});}
            var Q2;
            {var subQ0=sQuery(id+"F0.wireOp",EDGE,"E6");var subQ1=sQuery(id+"F0.wireOp",EDGE,"E0");var subQ2=makeQuery(id+"F0.imprint","INTERSECT",VERTEX,{"derivedFrom":[subQ1,subQ0]});Q2=makeQuery(id+"F0.imprint","IMPRINT",FACE,{"disambiguationData":[TD([[makeQuery(id+"F0.imprint","IMPRINT",EDGE,{"disambiguationData":[TD([[subQ2,-1.0]])],"derivedFrom":subQ1}),1.0]])]});}
            var Q3;
            {var subQ0=sQuery(id+"F0.wireOp",EDGE,"E7");var subQ1=sQuery(id+"F0.wireOp",EDGE,"E0");var subQ2=makeQuery(id+"F0.imprint","INTERSECT",VERTEX,{"derivedFrom":[subQ1,subQ0]});Q3=makeQuery(id+"F0.imprint","IMPRINT",FACE,{"disambiguationData":[TD([[makeQuery(id+"F0.imprint","IMPRINT",EDGE,{"disambiguationData":[TD([[subQ2,-1.0]])],"derivedFrom":subQ1}),1.0]])]});}
            extrude(context, id + "F31", {"entities" : qUnion([Q0, Q1, Q2, Q3]), "operationType" : NewBodyOperationType.ADD, "depth" : 2.54 * mm});
        }
    });
